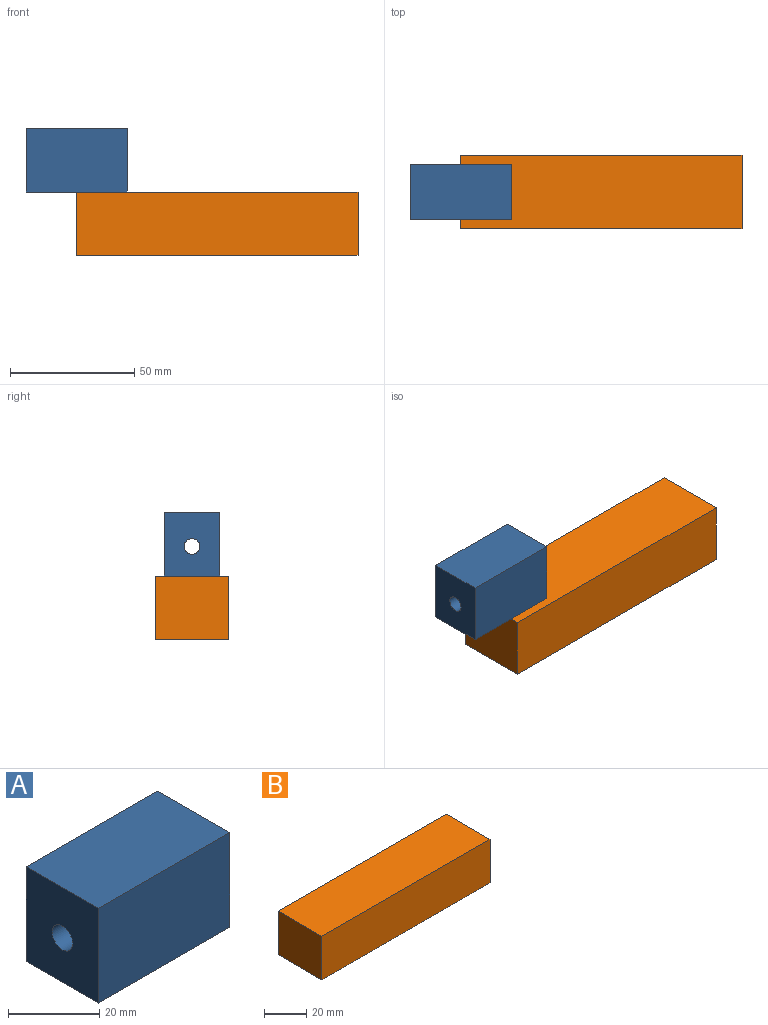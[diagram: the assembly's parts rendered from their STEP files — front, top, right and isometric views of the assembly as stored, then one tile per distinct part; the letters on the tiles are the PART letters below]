
ASSEMBLY  parts=2 mates=1
PART A: 7 faces, bbox 40.7x22.3x25.4 mm
  f0: plane 40.7x25.4mm, normal (0,-1,0), area 1033.7mm2, adj f1,f3,f4,f5
  f1: plane 25.4x22.34mm, normal (1,0,0), area 535.8mm2, adj f0,f2,f4,f5,f6
  f2: plane 40.7x25.4mm, normal (0,1,0), area 1033.7mm2, adj f1,f3,f4,f5
  f3: plane 25.4x22.34mm, normal (-1,0,0), area 535.8mm2, adj f0,f2,f4,f5,f6
  f4: plane 40.7x22.34mm, normal (0,0,1), area 909.2mm2, adj f0,f1,f2,f3
  f5: plane 40.7x22.34mm, normal (0,0,-1), area 909.2mm2, adj f0,f1,f2,f3
  f6: cylinder r=3.17mm len=40.7mm, axis (-1,0,0), area 811.9mm2, adj f1,f3
PART B: 6 faces, bbox 113.1x29.6x25.4 mm
  f0: plane 113.09x25.4mm, normal (0,-1,0), area 2872.4mm2, adj f1,f3,f4,f5
  f1: plane 29.61x25.4mm, normal (1,0,0), area 752.2mm2, adj f0,f2,f4,f5
  f2: plane 113.09x25.4mm, normal (0,1,0), area 2872.4mm2, adj f1,f3,f4,f5
  f3: plane 29.61x25.4mm, normal (-1,0,0), area 752.2mm2, adj f0,f2,f4,f5
  f4: plane 113.09x29.61mm, normal (0,0,1), area 3349mm2, adj f0,f1,f2,f3
  f5: plane 113.09x29.61mm, normal (0,0,-1), area 3349mm2, adj f0,f1,f2,f3
PLACE A t=(22.87,9.59,0.25)mm
PLACE B t=(115.61,5.95,-25.15)mm
MATE planar A.f5 <-> B.f4  axis (0,0,-1) through (2.53,20.76,0.25)mm
